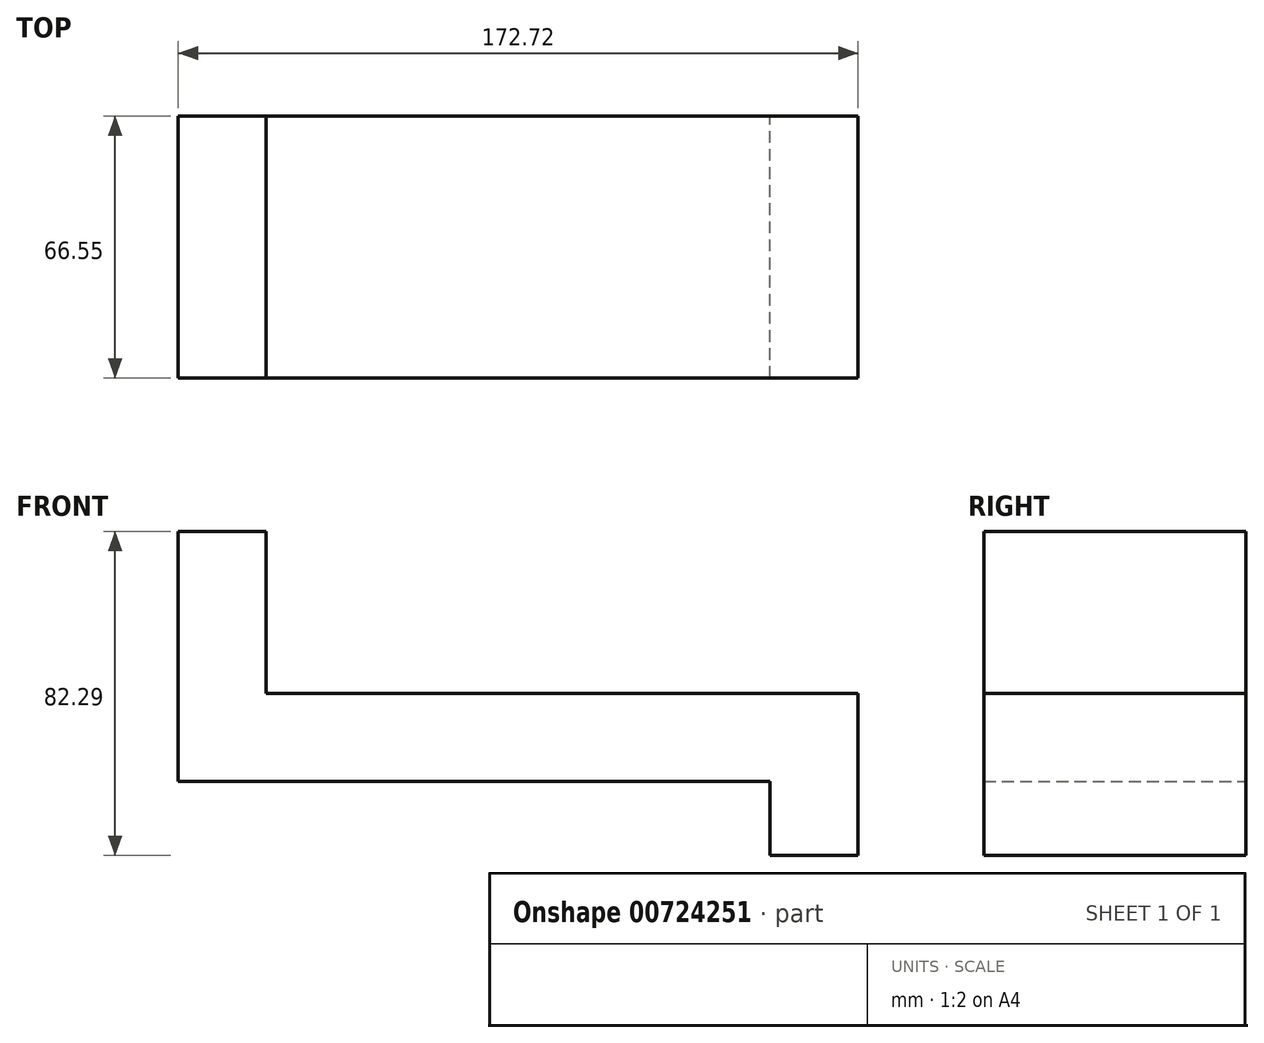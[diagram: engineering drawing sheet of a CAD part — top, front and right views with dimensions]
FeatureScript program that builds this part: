
annotation { "Feature Type Name" : "Feature", "Feature Type Description" : "" }
export const myFeature = defineFeature(function(context is Context, id is Id, definition is map)
    precondition{}
    {
        {
            var Q0;
            Q0=qCreatedBy(makeId("Front.planeOp"),FACE);
            var sketch = newSketch(context, id + "F0", { "sketchPlane" : qUnion([Q0])});
            skLineSegment(sketch, "E0", {"start": v(-76.1, 78.02) * mm, "end": v(-76.1, 14.52) * mm});
            skLineSegment(sketch, "E1", {"start": v(74.27, 14.52) * mm, "end": v(-76.1, 14.52) * mm});
            skLineSegment(sketch, "E2", {"start": v(74.27, -4.27) * mm, "end": v(74.27, 14.52) * mm});
            skLineSegment(sketch, "E3", {"start": v(74.27, -4.27) * mm, "end": v(96.62, -4.27) * mm});
            skLineSegment(sketch, "E4", {"start": v(96.62, -4.27) * mm, "end": v(96.62, 36.88) * mm});
            skLineSegment(sketch, "E5", {"start": v(96.62, 36.88) * mm, "end": v(-53.75, 36.88) * mm});
            skLineSegment(sketch, "E6", {"start": v(-53.75, 36.88) * mm, "end": v(-53.75, 78.02) * mm});
            skLineSegment(sketch, "E7", {"start": v(-53.75, 78.02) * mm, "end": v(-76.1, 78.02) * mm});
            skSolve(sketch);
        }
        {
            var Q0;
            Q0=makeQuery(id+"F0.imprint","IMPRINT",FACE,{"disambiguationData":[TD([[makeQuery(id+"F0.imprint","IMPRINT",EDGE,{"derivedFrom":sQuery(id+"F0.wireOp",EDGE,"E0")}),1.0]])]});
            extrude(context, id + "F1", {"entities" : qUnion([Q0]), "depth" : 66.55 * mm, "offsetDistance" : 25.4 * mm});
        }
    });
